AUTODESK INVENTOR PART (.ipt)
format: ipt  version: 2021 (Build 250183000, 183)  size: 569,344 bytes
history: native  units: mm
features: extrude x7, sketch x7, projected_geometry x6, chamfer x1, fillet x1
ambient origin geometry x8: Origin, YZ Plane, XZ Plane, XY Plane, X Axis, Y Axis, Z Axis, Center Point
bodies: Body1 (feature_tree)
feature tree (22):
  extrude  "Extrusion10"  Depth=7.5mm
  extrude  "Extrusion11"  Depth=11.0mm
  chamfer  "Chamfer2"  Distance=32.0mm
  extrude  "Extrusion12"  Depth=25.0mm
  extrude  "Extrusion13"  Depth=32.5mm
  extrude  "Extrusion14"  Depth=1.5mm
  extrude  "Extrusion15"  Depth=3.0mm TaperAngle=45.0deg
  extrude  "Extrusion16"  Depth=5.0mm
  fillet  "Fillet6"  Radius=1.5mm
  sketch  "Sketch10"  dims[d69=40.0mm d70=7.5mm]
  sketch  "Sketch11"  dims[d71=4.0mm d72=11.0mm d73=32.0mm d74=0.0mm]
  projected_geometry  "Projected Loop10"
  sketch  "Sketch12"  dims[d75=25.0mm d76=25.0mm]
  sketch  "Sketch13"  dims[d77=32.0mm d78=32.5mm]
  sketch  "Sketch15"  dims[d79=3.5mm d80=1.5mm]
  projected_geometry  "Projected Loop13"
  sketch  "Sketch16"  dims[d81=4.0mm d82=0.0mm d83=3.0mm d84=2.0mm d85=45.0deg]
  sketch  "Sketch17"  dims[d86=50.0mm d88=3.375mm d89=10.0mm d91=10.0mm d93=5.0mm d94=1.5mm d95=5.0mm d96=4.0mm d97=0.0mm d98=50.0mm d100=3.375mm d101=10.0mm d103=10.0mm d105=5.0mm d106=1.5mm d107=5.0mm d108=4.0mm d109=0.0mm d118=30.0mm d120=3.6mm d121=10.0mm d123=10.0mm d125=2.5mm d126=2.4mm d127=3.0mm d128=8.0mm d129=1.5mm d130=3.0mm d131=5.0mm d132=2.5mm d134=4.0mm d135=10.0mm d136=0.0mm d137=1.5mm d138=27.0mm d139=32.0mm d140=2.5mm d141=38.0mm d142=0.0mm d143=14.0mm d144=3.4mm d145=7.2mm d146=2.0mm d147=3.0mm d148=3.0mm d149=25.0mm d150=25.0mm d151=20.0mm d153=19.0mm d154=20.0mm d156=19.0mm d159=38.0mm d160=0.0mm d162=0.3mm]
  projected_geometry  "Projected Loop14"
  projected_geometry  "Projected Loop15"
  projected_geometry  "Projected Loop16"
  projected_geometry  "Projected Loop17"
